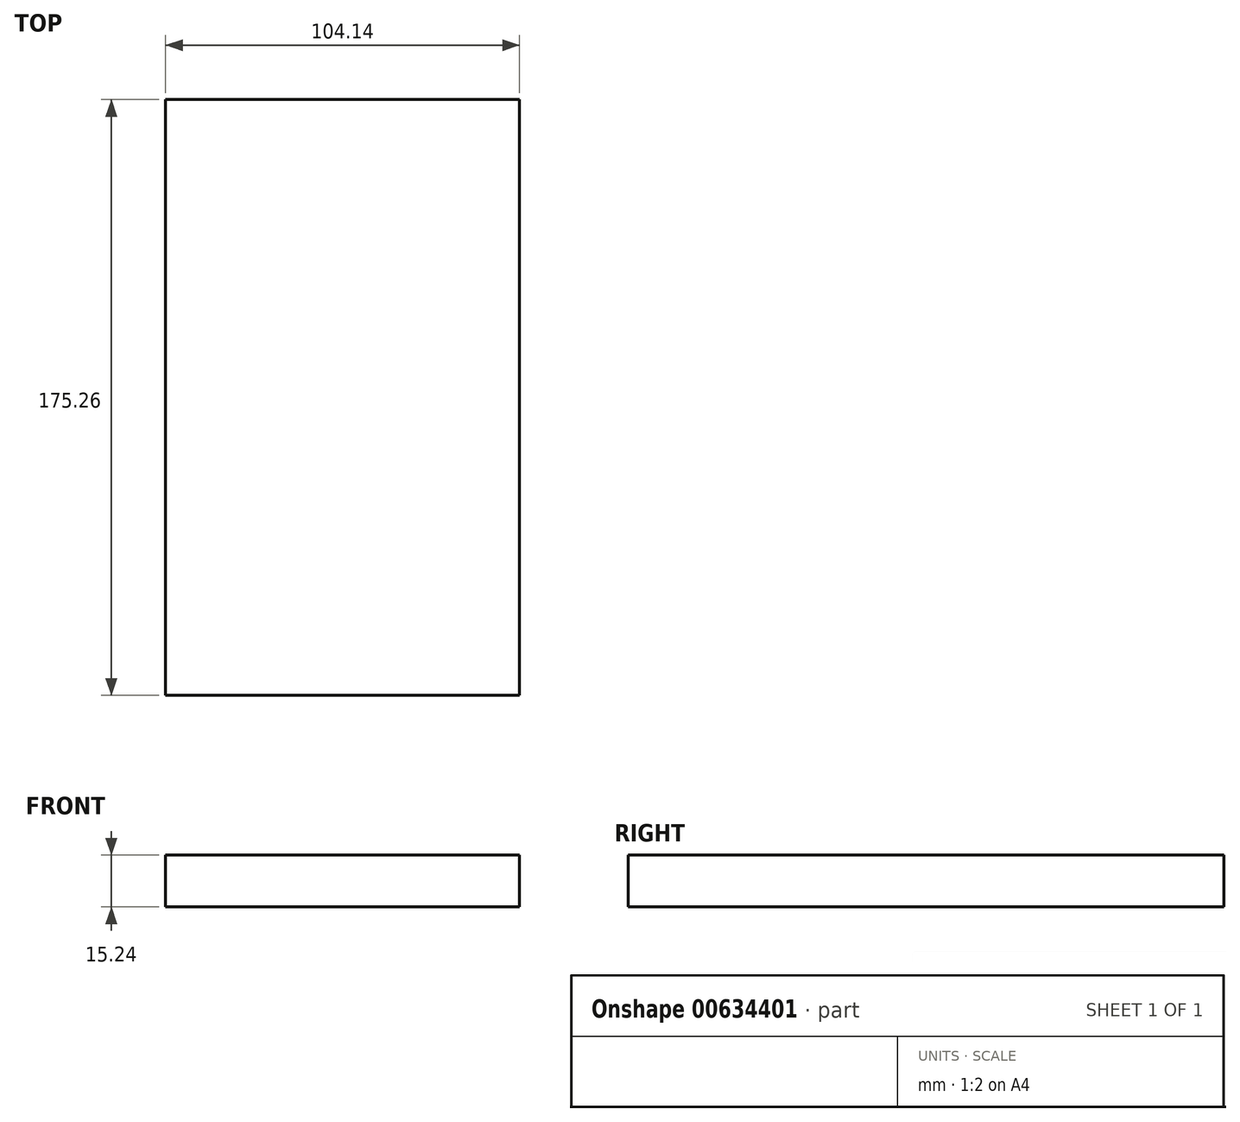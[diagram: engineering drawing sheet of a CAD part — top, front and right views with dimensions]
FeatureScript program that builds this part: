
annotation { "Feature Type Name" : "Feature", "Feature Type Description" : "" }
export const myFeature = defineFeature(function(context is Context, id is Id, definition is map)
    precondition{}
    {
        {
            var Q0;
            Q0=qCreatedBy(makeId("Top.planeOp"),FACE);
            var sketch = newSketch(context, id + "F0", { "sketchPlane" : qUnion([Q0])});
            skLineSegment(sketch, "E0.bottom", {"start": v(-52.07, 87.63) * mm, "end": v(52.07, 87.63) * mm});
            skLineSegment(sketch, "E0.top", {"start": v(-52.07, -87.63) * mm, "end": v(52.07, -87.63) * mm});
            skLineSegment(sketch, "E0.left", {"start": v(-52.07, 87.63) * mm, "end": v(-52.07, -87.63) * mm});
            skLineSegment(sketch, "E0.right", {"start": v(52.07, 87.63) * mm, "end": v(52.07, -87.63) * mm});
            skPoint(sketch, "E0.middle", {"position": v(0, 0) * mm});
            skSolve(sketch);
        }
        {
            var Q0;
            Q0 = qSketchRegion(id + "F0", true);
            extrude(context, id + "F1", {"entities" : qUnion([Q0]), "depth" : 15.24 * mm, "offsetDistance" : 25.4 * mm});
        }
    });
